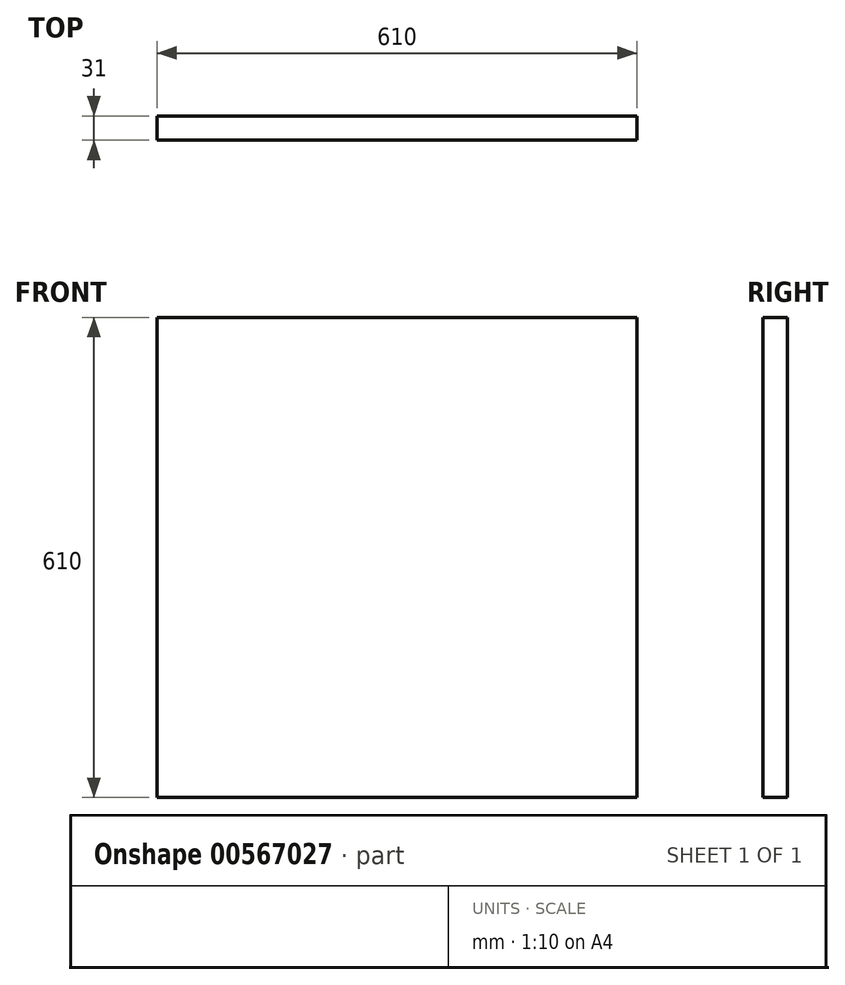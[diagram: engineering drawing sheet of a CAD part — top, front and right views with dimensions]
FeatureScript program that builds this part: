
annotation { "Feature Type Name" : "Feature", "Feature Type Description" : "" }
export const myFeature = defineFeature(function(context is Context, id is Id, definition is map)
    precondition{}
    {
        {
            var Q0;
            Q0=qCreatedBy(makeId("Front.planeOp"),FACE);
            var sketch = newSketch(context, id + "F0", { "sketchPlane" : qUnion([Q0])});
            skLineSegment(sketch, "E0.bottom", {"start": v(-572.32, 358.02) * mm, "end": v(37.68, 358.02) * mm});
            skLineSegment(sketch, "E0.top", {"start": v(-572.32, -251.98) * mm, "end": v(37.68, -251.98) * mm});
            skLineSegment(sketch, "E0.left", {"start": v(-572.32, 358.02) * mm, "end": v(-572.32, -251.98) * mm});
            skLineSegment(sketch, "E0.right", {"start": v(37.68, 358.02) * mm, "end": v(37.68, -251.98) * mm});
            skSolve(sketch);
        }
        {
            var Q0;
            Q0 = qSketchRegion(id + "F0", true);
            extrude(context, id + "F1", {"entities" : qUnion([Q0]), "depth" : 31 * mm, "offsetDistance" : 25 * mm});
        }
    });
